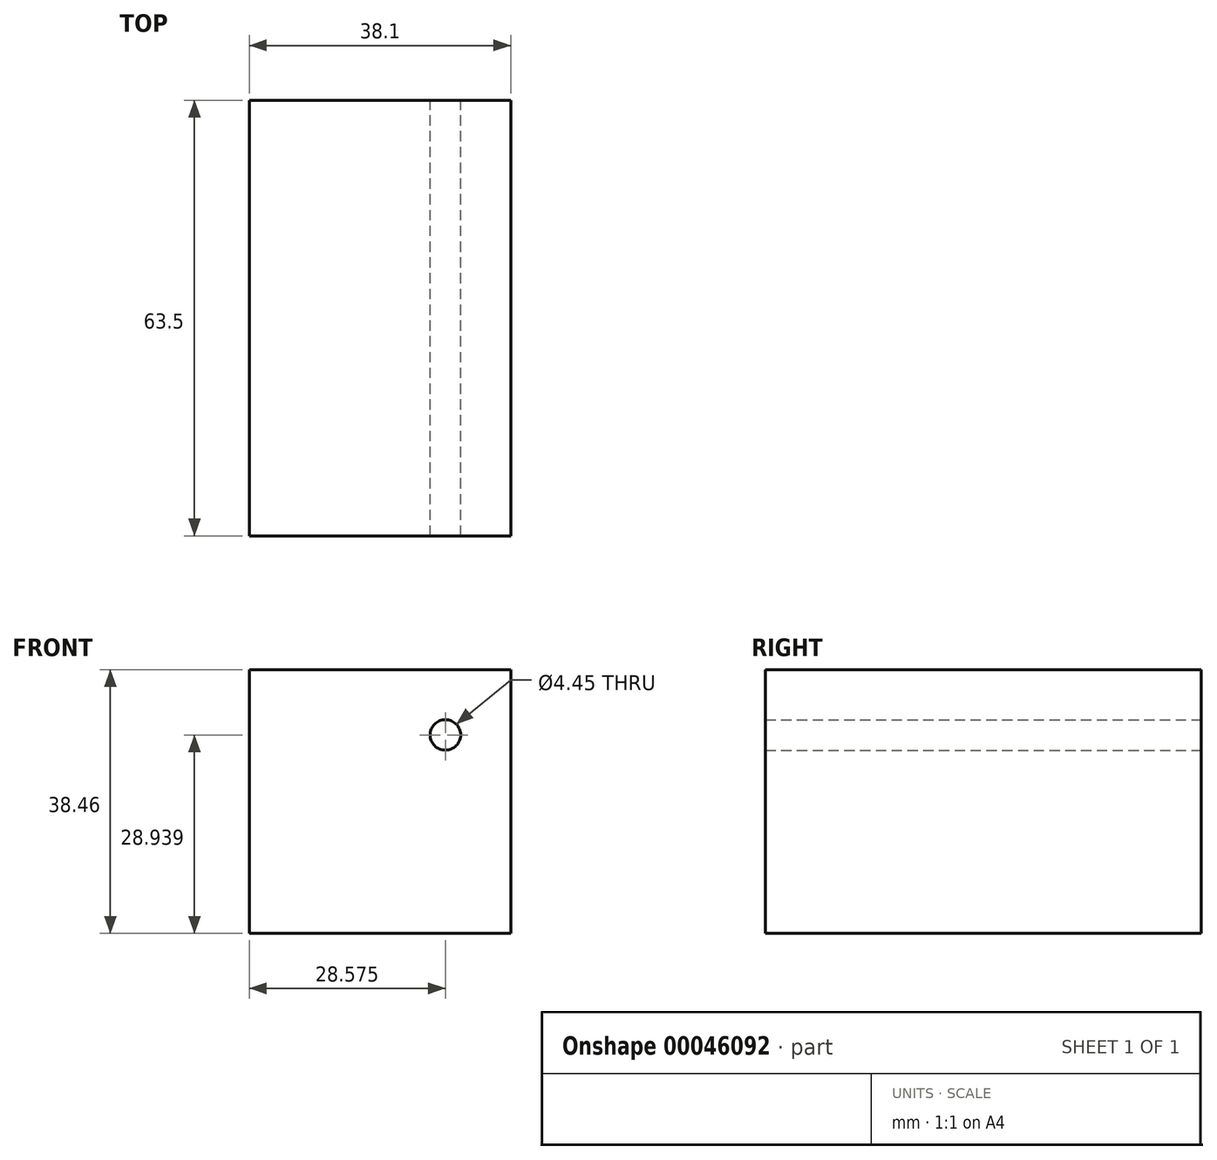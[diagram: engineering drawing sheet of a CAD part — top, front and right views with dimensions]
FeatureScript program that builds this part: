
annotation { "Feature Type Name" : "Feature", "Feature Type Description" : "" }
export const myFeature = defineFeature(function(context is Context, id is Id, definition is map)
    precondition{}
    {
        {
            var Q0;
            Q0=qCreatedBy(makeId("Front.planeOp"),FACE);
            var sketch = newSketch(context, id + "F0", { "sketchPlane" : qUnion([Q0])});
            skLineSegment(sketch, "E0.rect.bottom", {"start": v(19.05, -19.23) * mm, "end": v(-19.05, -19.23) * mm});
            skLineSegment(sketch, "E0.rect.top", {"start": v(19.05, 19.23) * mm, "end": v(-19.05, 19.23) * mm});
            skLineSegment(sketch, "E0.rect.left", {"start": v(19.05, -19.23) * mm, "end": v(19.05, 19.23) * mm});
            skLineSegment(sketch, "E0.rect.right", {"start": v(-19.05, -19.23) * mm, "end": v(-19.05, 19.23) * mm});
            skPoint(sketch, "E0.rect.middle", {"position": v(0, 0) * mm});
            skCircle(sketch, "E1", {"center": v(9.52, 9.7) * mm, "radius": 2.22 * mm});
            skLineSegment(sketch, "E2", {"start": v(9.52, 9.7) * mm, "end": v(19.05, 9.7) * mm, "construction": true});
            skLineSegment(sketch, "E3", {"start": v(9.53, 9.7) * mm, "end": v(9.53, 19.23) * mm, "construction": true});
            skSolve(sketch);
        }
        {
            var Q0;
            Q0=makeQuery(id+"F0.imprint","IMPRINT",FACE,{"disambiguationData":[TD([[makeQuery(id+"F0.imprint","IMPRINT",EDGE,{"derivedFrom":sQuery(id+"F0.wireOp",EDGE,"E0.rect.bottom")}),-1.0]])]});
            extrude(context, id + "F1", {"entities" : qUnion([Q0]), "depth" : 63.5 * mm});
        }
    });
